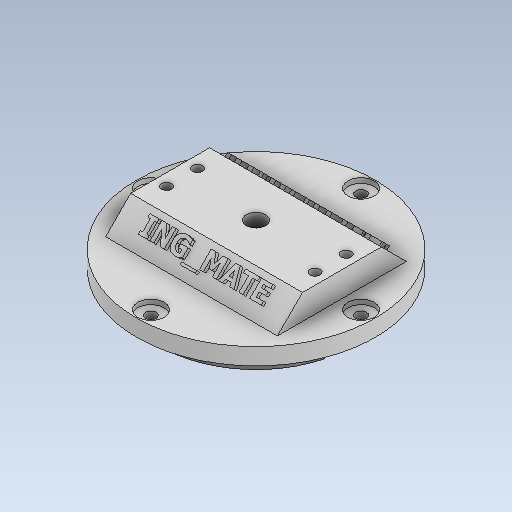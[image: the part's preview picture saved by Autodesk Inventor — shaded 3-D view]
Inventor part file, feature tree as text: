
AUTODESK INVENTOR PART (.ipt)
format: ipt  version: 2021 (Build 250183000, 183)  size: 548,864 bytes
history: native  units: mm
features: extrude x9, sketch x9, chamfer x3
ambient origin geometry x8: Origin, YZ Plane, XZ Plane, XY Plane, X Axis, Y Axis, Z Axis, Center Point
bodies: Solid1 (feature_tree)
feature tree (21):
  extrude  "Extrusion1"  Depth=8.1mm
  extrude  "Extrusion2"  Depth=4.5mm
  extrude  "Extrusion7"  Depth=4.5mm
  chamfer  "Chamfer1"  Distance=44.0mm
  extrude  "Extrusion9"  Depth=1.5mm
  chamfer  "Chamfer2"  Distance=7.0mm
  extrude  "Extrusion10"  Depth=1.5mm
  extrude  "Extrusion11"  Depth=1.5mm TaperAngle=0.0deg
  chamfer  "Chamfer3"  Distance=25.5mm
  extrude  "Extrusion12"  Depth=1.5mm TaperAngle=0.0deg
  extrude  "Extrusion13"  Depth=1.5mm TaperAngle=45.0deg
  extrude  "Extrusion14"  Depth=1.5mm
  sketch  "Sketch1"  dims[d0=100.0mm d1=8.1mm]
  sketch  "Sketch2"  dims[d2=4.5mm d3=4.5mm]
  sketch  "Sketch7"  dims[d4=4.5mm d5=4.5mm]
  sketch  "Sketch11"  dims[d6=88.0mm]
  sketch  "Sketch12"  dims[d7=88.0mm]
  sketch  "Sketch13"  dims[d8=0.0mm]
  sketch  "Sketch14"  dims[d9=0.0mm]
  sketch  "Sketch15"  dims[d10=0.0mm]
  sketch  "Sketch16"  dims[d11=0.0mm d12=44.0mm d13=44.0mm d14=7.0mm d15=0.0mm d16=79.8mm d17=8.5mm d18=0.0mm d30=25.5mm d31=6.0mm d32=0.0mm d33=6.0mm d34=2.0mm d35=45.0deg d39=71.921mm d40=33.0mm d41=35.9605mm d42=16.5mm d43=4.2mm d44=4.2mm d45=4.2mm d46=4.2mm d47=13.0mm d48=13.0mm d49=62.2mm d50=62.2mm d51=5.0mm d52=10.0mm d53=10.0mm d54=10.0mm d55=10.5mm d56=0.0mm d57=10.5mm d58=2.0mm d59=45.0deg d60=0.0mm d61=0.0mm d62=7.0mm d63=7.0mm d64=7.0mm d65=7.0mm d66=10.0mm d67=0.0mm d68=2.0mm d69=2.0mm d70=45.0deg d71=11.0mm d72=11.0mm d73=11.0mm d74=11.0mm d75=2.0mm d76=0.0mm d77=1.5mm d78=0.0mm d79=1.5mm d80=0.0mm]
